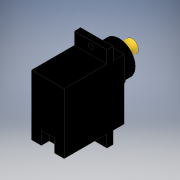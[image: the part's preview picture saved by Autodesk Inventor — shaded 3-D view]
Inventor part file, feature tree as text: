
AUTODESK INVENTOR PART (.ipt)
format: ipt  version: 2018 (Build 220112000, 112)  size: 202,752 bytes
history: native  units: mm
features: extrude x7, sketch x7, other x3
ambient origin geometry x8: Origin, YZ Plane, XZ Plane, XY Plane, X Axis, Y Axis, Z Axis, Center Point
bodies: Body1 (feature_tree)
feature tree (17):
  other  "Sólido1"
  extrude  "Extrusión1"  Depth=23.2mm
  extrude  "Extrusión2"  Depth=16.4mm
  other  "Edición directa1"
  extrude  "Extrusión3"  Depth=2.4mm
  extrude  "Extrusión4"  Depth=11.8mm TaperAngle=0.0deg
  extrude  "Extrusión5"  Depth=0.7mm
  extrude  "Extrusión6"  Depth=2.0mm
  extrude  "Extrusión7"  Depth=2.4mm TaperAngle=0.0deg
  sketch  "Boceto1"  dims[d0=11.8mm d1=23.2mm]
  sketch  "Boceto2"  dims[d2=23.0mm d3=0.0mm d4=16.4mm]
  sketch  "Boceto4"  dims[d5=4.7mm d6=2.4mm]
  sketch  "Boceto5"  dims[d7=4.7mm d8=11.8mm d9=0.0mm]
  sketch  "Boceto6"  dims[d10=0.0mm d11=0.0mm d12=0.7mm d13=1.9mm]
  sketch  "Boceto7"  dims[d14=1.9mm d15=2.0mm]
  sketch  "Boceto8"  dims[d16=2.0mm d17=2.4mm d18=0.0mm d19=15.0mm d20=4.3mm d21=0.0mm d22=5.0mm d23=4.8mm d24=5.0mm d25=0.0mm d26=6.25mm d28=4.3mm d29=0.0mm d30=3.0mm d31=2.5mm d32=2.5mm d33=5.0mm d34=0.0mm]
  other  "Desplazar1"
